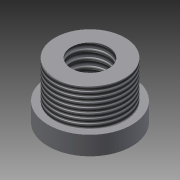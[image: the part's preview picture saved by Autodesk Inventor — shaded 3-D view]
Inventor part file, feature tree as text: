
AUTODESK INVENTOR PART (.ipt)
format: ipt  version: 2013 (Build 170138000, 138)  size: 100,864 bytes
history: native  units: in
note: dims shown in document units (in); Inventor stores cm internally (conversion verified against a paired STEP export)
features: extrude x3, sketch x3, thread x2
ambient origin geometry x8: Origin, YZ Plane, XZ Plane, XY Plane, X Axis, Y Axis, Z Axis, Center Point
bodies: Solid1 (feature_tree)
feature tree (8):
  extrude  "Extrusion1"  Depth=0.25in TaperAngle=0.0deg
  extrude  "Extrusion2"  Depth=0.5in TaperAngle=0.0deg
  extrude  "Extrusion3"  Depth=100.0in TaperAngle=0.0deg
  thread  "Thread1"  [1 undecoded]
  thread  "Thread2"  [1 undecoded]
  sketch  "Sketch1"  dims[d0=1.12in d1=0.25in d2=0.0in]
  sketch  "Sketch2"  dims[d3=0.937in d4=0.5in d5=0.0in]
  sketch  "Sketch3"  dims[d6=0.5in d7=100.0in d8=0.0in d9=1.0in d10=0.0in d11=1.0in d12=0.0in]
note: 2 required parameter values undecoded (feature->parameter linkage not recoverable at this tier; creation-order binding heuristic only, values carry confidence <= 0.55)
